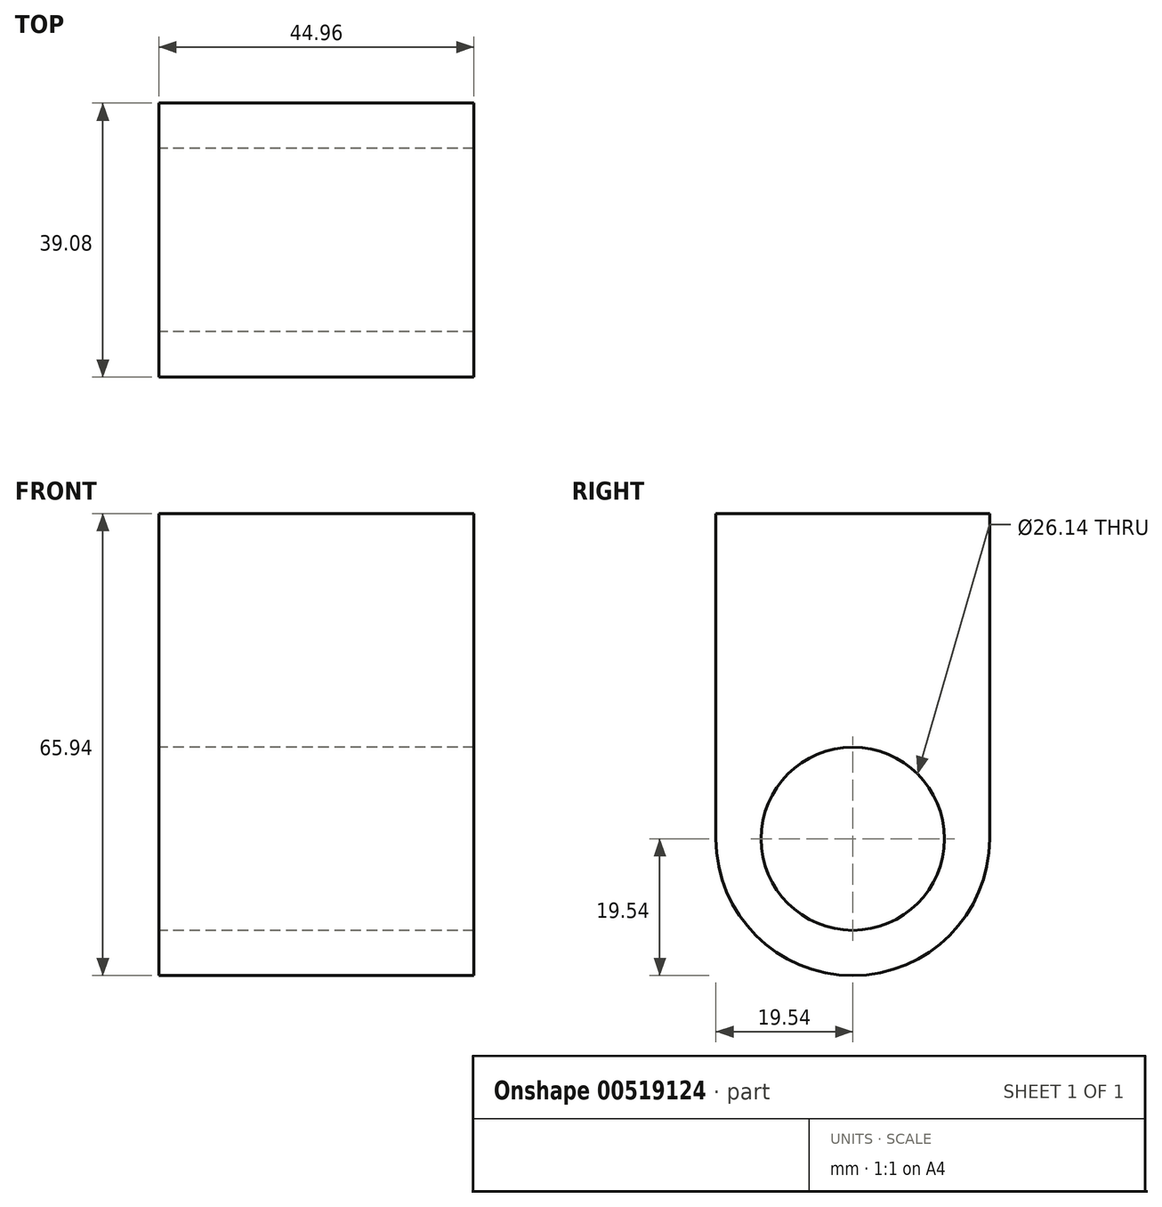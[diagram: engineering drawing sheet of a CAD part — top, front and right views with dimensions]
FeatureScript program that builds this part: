
annotation { "Feature Type Name" : "Feature", "Feature Type Description" : "" }
export const myFeature = defineFeature(function(context is Context, id is Id, definition is map)
    precondition{}
    {
        {
            var Q0;
            Q0=qCreatedBy(makeId("Right.planeOp"),FACE);
            var sketch = newSketch(context, id + "F0", { "sketchPlane" : qUnion([Q0])});
            skLineSegment(sketch, "E0.bottom", {"start": v(-19.54, -23.2) * mm, "end": v(19.54, -23.2) * mm});
            skLineSegment(sketch, "E0.top", {"start": v(-19.54, 23.2) * mm, "end": v(19.54, 23.2) * mm});
            skLineSegment(sketch, "E0.left", {"start": v(-19.54, -23.2) * mm, "end": v(-19.54, 23.2) * mm});
            skLineSegment(sketch, "E0.right", {"start": v(19.54, -23.2) * mm, "end": v(19.54, 23.2) * mm});
            skPoint(sketch, "E0.middle", {"position": v(0, 0) * mm});
            skCircle(sketch, "E1", {"center": v(0, -23.2) * mm, "radius": 19.54 * mm});
            skCircle(sketch, "E2.0", {"center": v(0, -23.2) * mm, "radius": 13.07 * mm});
            skSolve(sketch);
        }
        {
            var Q0;
            {var subQ0=sQuery(id+"F0.wireOp",EDGE,"E1");var subQ1=sQuery(id+"F0.wireOp",EDGE,"E0.bottom");var subQ2=makeQuery(id+"F0.imprint","INTERSECT",VERTEX,{"disambiguationData":[OD(0.0)],"derivedFrom":[subQ1,subQ0]});Q0=makeQuery(id+"F0.imprint","IMPRINT",FACE,{"disambiguationData":[TD([[makeQuery(id+"F0.imprint","IMPRINT",EDGE,{"disambiguationData":[TD([[subQ2,-1.0]])],"derivedFrom":subQ1}),-1.0]])]});}
            var Q1;
            {var subQ0=sQuery(id+"F0.wireOp",EDGE,"E1");var subQ1=sQuery(id+"F0.wireOp",EDGE,"E0.bottom");var subQ2=makeQuery(id+"F0.imprint","INTERSECT",VERTEX,{"disambiguationData":[OD(0.0)],"derivedFrom":[subQ1,subQ0]});Q1=makeQuery(id+"F0.imprint","IMPRINT",FACE,{"disambiguationData":[TD([[makeQuery(id+"F0.imprint","IMPRINT",EDGE,{"disambiguationData":[TD([[subQ2,-1.0]])],"derivedFrom":subQ1}),1.0]])]});}
            var Q2;
            Q2=makeQuery(id+"F0.imprint","IMPRINT",FACE,{"disambiguationData":[TD([[makeQuery(id+"F0.imprint","IMPRINT",EDGE,{"derivedFrom":sQuery(id+"F0.wireOp",EDGE,"E0.top")}),-1.0]])]});
            extrude(context, id + "F1", {"entities" : qUnion([Q0, Q1, Q2]), "depth" : 44.96 * mm});
        }
    });
